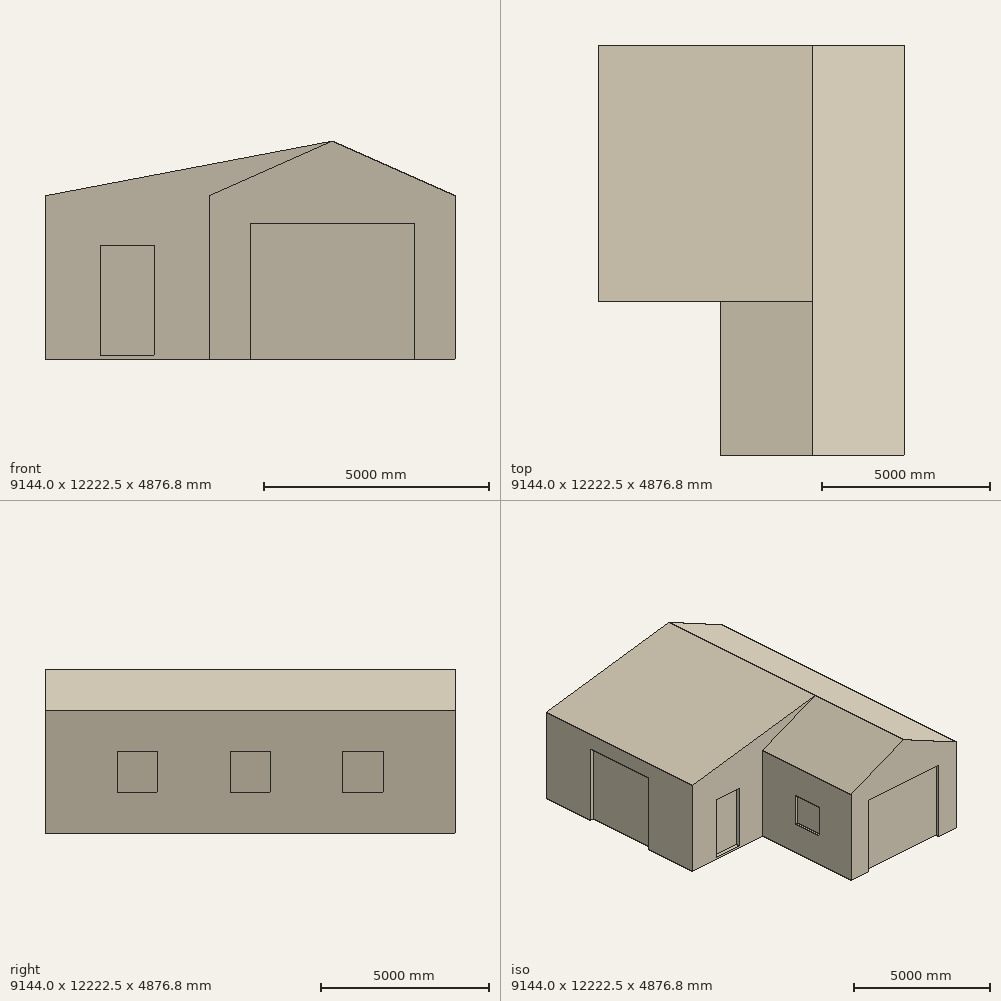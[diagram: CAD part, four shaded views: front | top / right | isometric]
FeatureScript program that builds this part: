
annotation { "Feature Type Name" : "Feature", "Feature Type Description" : "" }
export const myFeature = defineFeature(function(context is Context, id is Id, definition is map)
    precondition{}
    {
        {
            var Q0;
            Q0=qCreatedBy(makeId("Front.planeOp"),FACE);
            var sketch = newSketch(context, id + "F0", { "sketchPlane" : qUnion([Q0])});
            skLineSegment(sketch, "E0", {"start": v(0, 0) * mm, "end": v(5486.4, 0) * mm});
            skLineSegment(sketch, "E1", {"start": v(5486.4, 0) * mm, "end": v(5486.4, 3657.6) * mm});
            skLineSegment(sketch, "E2", {"start": v(5486.4, 3657.6) * mm, "end": v(2743.2, 4876.8) * mm});
            skLineSegment(sketch, "E3", {"start": v(2743.2, 4876.8) * mm, "end": v(0, 3657.6) * mm});
            skLineSegment(sketch, "E4", {"start": v(0, 3657.6) * mm, "end": v(0, 0) * mm});
            skPoint(sketch, "E5", {"position": v(2743.2, 0) * mm});
            skSolve(sketch);
        }
        {
            var Q0;
            Q0=makeQuery(id+"F0.imprint","IMPRINT",FACE,{"disambiguationData":[TD([[makeQuery(id+"F0.imprint","IMPRINT",EDGE,{"derivedFrom":sQuery(id+"F0.wireOp",EDGE,"E0")}),1.0]])]});
            extrude(context, id + "F1", {"entities" : qUnion([Q0]), "depth" : 12192 * mm, "offsetDistance" : 30.48 * mm});
        }
        {
            var Q0;
            Q0=makeQuery(id+"F1.opExtrude","SWEPT_FACE",FACE,{"disambiguationData":[OSD([sQuery(id+"F0.wireOp",EDGE,"E4")])]});
            var sketch = newSketch(context, id + "F2", { "sketchPlane" : qUnion([Q0])});
            skLineSegment(sketch, "E6", {"start": v(0, 0) * mm, "end": v(0, 3657.6) * mm});
            skLineSegment(sketch, "E7.0", {"start": v(12192, 4876.8) * mm, "end": v(3810, 4876.8) * mm});
            skLineSegment(sketch, "E8", {"start": v(7620, 3657.6) * mm, "end": v(7620, 0) * mm});
            skLineSegment(sketch, "E9", {"start": v(7620, 0) * mm, "end": v(0, 0) * mm});
            skPoint(sketch, "E10", {"position": v(3810, 0) * mm});
            skLineSegment(sketch, "E11", {"start": v(0, 3657.6) * mm, "end": v(7620, 3657.6) * mm});
            skPoint(sketch, "E12.start.orphan", {"position": v(3810, 4876.8) * mm});
            skPoint(sketch, "E13.orphan", {"position": v(0, 4876.8) * mm});
            skSolve(sketch);
        }
        {
            var Q0;
            Q0=qSketchRegion(id+"F2",true);
            extrude(context, id + "F3", {"entities" : qUnion([Q0]), "operationType" : NewBodyOperationType.ADD, "depth" : 3657.6 * mm, "offsetDistance" : 30.48 * mm, "hasSecondDirection" : true, "secondDirectionOppositeDirection" : true, "secondDirectionDepth" : 2743.2 * mm});
        }
        {
            var Q0;
            Q0=makeQuery(id+"F1.opExtrude","CAP_FACE",FACE,{"disambiguationData":[OSD([sQuery(id+"F0.wireOp",EDGE,"E0"),sQuery(id+"F0.wireOp",EDGE,"E1"),sQuery(id+"F0.wireOp",EDGE,"E2"),sQuery(id+"F0.wireOp",EDGE,"E3"),sQuery(id+"F0.wireOp",EDGE,"E4")])],"isStart":false});
            extrude(context, id + "F4", {"entities" : qUnion([Q0]), "operationType" : NewBodyOperationType.ADD, "depth" : 30.48 * mm, "offsetDistance" : 30.48 * mm});
        }
        {
            var Q0;
            Q0=makeQuery(id+"F4.opExtrude","CAP_FACE",FACE,{"disambiguationData":[OSD([sQuery(id+"F0.wireOp",EDGE,"E0"),sQuery(id+"F0.wireOp",EDGE,"E1"),sQuery(id+"F0.wireOp",EDGE,"E2"),sQuery(id+"F0.wireOp",EDGE,"E3"),sQuery(id+"F0.wireOp",EDGE,"E4")])],"isStart":false});
            var sketch = newSketch(context, id + "F5", { "sketchPlane" : qUnion([Q0])});
            skLineSegment(sketch, "E14.bottom", {"start": v(914.4, 0) * mm, "end": v(4572, 0) * mm});
            skLineSegment(sketch, "E14.top", {"start": v(914.4, 3048) * mm, "end": v(4572, 3048) * mm});
            skLineSegment(sketch, "E14.left", {"start": v(914.4, 0) * mm, "end": v(914.4, 3048) * mm});
            skLineSegment(sketch, "E14.right", {"start": v(4572, 0) * mm, "end": v(4572, 3048) * mm});
            skSolve(sketch);
        }
        {
            var Q0;
            Q0=qSketchRegion(id+"F5",true);
            extrude(context, id + "F6", {"entities" : qUnion([Q0]), "operationType" : NewBodyOperationType.REMOVE, "oppositeDirection" : true, "depth" : 152.4 * mm, "offsetDistance" : 30.48 * mm});
        }
        {
            var Q0;
            Q0=makeQuery(id+"F3.opExtrude","CAP_FACE",FACE,{"disambiguationData":[OSD([sQuery(id+"F2.wireOp",EDGE,"E6"),sQuery(id+"F2.wireOp",EDGE,"TFXyKFC6-9P5i-MGsC-qPEY-CPmH8dyxXZE2"),sQuery(id+"F2.wireOp",EDGE,"E12"),sQuery(id+"F2.wireOp",EDGE,"E8"),sQuery(id+"F2.wireOp",EDGE,"E9")])],"isStart":false});
            var sketch = newSketch(context, id + "F7", { "sketchPlane" : qUnion([Q0])});
            skLineSegment(sketch, "E15.bottom", {"start": v(2286, 0) * mm, "end": v(5334, 0) * mm});
            skLineSegment(sketch, "E15.top", {"start": v(2286, 3048) * mm, "end": v(5334, 3048) * mm});
            skLineSegment(sketch, "E15.left", {"start": v(2286, 0) * mm, "end": v(2286, 3048) * mm});
            skLineSegment(sketch, "E15.right", {"start": v(5334, 0) * mm, "end": v(5334, 3048) * mm});
            skSolve(sketch);
        }
        {
            var Q0;
            Q0=qSketchRegion(id+"F7",true);
            extrude(context, id + "F8", {"entities" : qUnion([Q0]), "operationType" : NewBodyOperationType.REMOVE, "oppositeDirection" : true, "depth" : 152.4 * mm, "offsetDistance" : 30.48 * mm});
        }
        {
            var Q0;
            Q0=makeQuery(id+"F3.opExtrude","SWEPT_FACE",FACE,{"disambiguationData":[OSD([sQuery(id+"F2.wireOp",EDGE,"E8")])]});
            var sketch = newSketch(context, id + "F9", { "sketchPlane" : qUnion([Q0])});
            skLineSegment(sketch, "E16.bottom", {"start": v(-2438.4, 100.58) * mm, "end": v(-1219.2, 100.58) * mm});
            skLineSegment(sketch, "E16.top", {"start": v(-2438.4, 2538.98) * mm, "end": v(-1219.2, 2538.98) * mm});
            skLineSegment(sketch, "E16.left", {"start": v(-2438.4, 100.58) * mm, "end": v(-2438.4, 2538.98) * mm});
            skLineSegment(sketch, "E16.right", {"start": v(-1219.2, 100.58) * mm, "end": v(-1219.2, 2538.98) * mm});
            skSolve(sketch);
        }
        {
            var Q0;
            Q0=qSketchRegion(id+"F9",true);
            extrude(context, id + "F10", {"entities" : qUnion([Q0]), "operationType" : NewBodyOperationType.REMOVE, "oppositeDirection" : true, "depth" : 152.4 * mm, "offsetDistance" : 30.48 * mm});
        }
        {
            var Q0;
            {var subQ0=sQuery(id+"F0.wireOp",EDGE,"E1");Q0=makeQuery(id+"F4.boolean.opBoolean","MERGE",FACE,{"derivedFrom":[makeQuery(id+"F1.opExtrude","SWEPT_FACE",FACE,{"disambiguationData":[OSD([subQ0])]}),makeQuery(id+"F4.opExtrude","SWEPT_FACE",FACE,{"disambiguationData":[OSD([subQ0])]})]});}
            var sketch = newSketch(context, id + "F11", { "sketchPlane" : qUnion([Q0])});
            skLineSegment(sketch, "E17.bottom", {"start": v(-10088.88, 2438.4) * mm, "end": v(-8869.68, 2438.4) * mm});
            skLineSegment(sketch, "E17.top", {"start": v(-10088.88, 1219.2) * mm, "end": v(-8869.68, 1219.2) * mm});
            skLineSegment(sketch, "E17.left", {"start": v(-10088.88, 2438.4) * mm, "end": v(-10088.88, 1219.2) * mm});
            skLineSegment(sketch, "E17.right", {"start": v(-8869.68, 2438.4) * mm, "end": v(-8869.68, 1219.2) * mm});
            skLineSegment(sketch, "E18.bottom", {"start": v(-6720.84, 2438.4) * mm, "end": v(-5501.64, 2438.4) * mm});
            skLineSegment(sketch, "E18.top", {"start": v(-6720.84, 1219.2) * mm, "end": v(-5501.64, 1219.2) * mm});
            skLineSegment(sketch, "E18.left", {"start": v(-6720.84, 2438.4) * mm, "end": v(-6720.84, 1219.2) * mm});
            skLineSegment(sketch, "E18.right", {"start": v(-5501.64, 2438.4) * mm, "end": v(-5501.64, 1219.2) * mm});
            skLineSegment(sketch, "E19.bottom", {"start": v(-3368.04, 2438.4) * mm, "end": v(-2148.84, 2438.4) * mm});
            skLineSegment(sketch, "E19.top", {"start": v(-3368.04, 1219.2) * mm, "end": v(-2148.84, 1219.2) * mm});
            skLineSegment(sketch, "E19.left", {"start": v(-3368.04, 2438.4) * mm, "end": v(-3368.04, 1219.2) * mm});
            skLineSegment(sketch, "E19.right", {"start": v(-2148.84, 2438.4) * mm, "end": v(-2148.84, 1219.2) * mm});
            skPoint(sketch, "E20", {"position": v(-6111.24, 2438.4) * mm});
            skPoint(sketch, "E21", {"position": v(-6111.24, 3657.6) * mm});
            skSolve(sketch);
        }
        {
            var Q0;
            Q0=qSketchRegion(id+"F11",true);
            extrude(context, id + "F12", {"entities" : qUnion([Q0]), "operationType" : NewBodyOperationType.REMOVE, "oppositeDirection" : true, "depth" : 100.58 * mm, "offsetDistance" : 30.48 * mm});
        }
        {
            var Q0;
            Q0=makeQuery(id+"F3.boolean.opBoolean","MERGE",FACE,{"derivedFrom":[makeQuery(id+"F1.opExtrude","CAP_FACE",FACE,{"disambiguationData":[OSD([sQuery(id+"F0.wireOp",EDGE,"E0"),sQuery(id+"F0.wireOp",EDGE,"E1"),sQuery(id+"F0.wireOp",EDGE,"E2"),sQuery(id+"F0.wireOp",EDGE,"E3"),sQuery(id+"F0.wireOp",EDGE,"E4")])],"isStart":true}),makeQuery(id+"F3.opExtrude","SWEPT_FACE",FACE,{"disambiguationData":[OSD([sQuery(id+"F2.wireOp",EDGE,"E6")])]})]});
            var sketch = newSketch(context, id + "F13", { "sketchPlane" : qUnion([Q0])});
            skLineSegment(sketch, "E22.bottom", {"start": v(-3352.8, 2438.4) * mm, "end": v(-2133.6, 2438.4) * mm});
            skLineSegment(sketch, "E22.top", {"start": v(-3352.8, 1219.2) * mm, "end": v(-2133.6, 1219.2) * mm});
            skLineSegment(sketch, "E22.left", {"start": v(-3352.8, 2438.4) * mm, "end": v(-3352.8, 1219.2) * mm});
            skLineSegment(sketch, "E22.right", {"start": v(-2133.6, 2438.4) * mm, "end": v(-2133.6, 1219.2) * mm});
            skLineSegment(sketch, "E23.bottom", {"start": v(914.4, 2438.4) * mm, "end": v(2133.6, 2438.4) * mm});
            skLineSegment(sketch, "E23.top", {"start": v(914.4, 1219.2) * mm, "end": v(2133.6, 1219.2) * mm});
            skLineSegment(sketch, "E23.left", {"start": v(914.4, 2438.4) * mm, "end": v(914.4, 1219.2) * mm});
            skLineSegment(sketch, "E23.right", {"start": v(2133.6, 2438.4) * mm, "end": v(2133.6, 1219.2) * mm});
            skPoint(sketch, "E24", {"position": v(-2743.2, 2438.4) * mm});
            skPoint(sketch, "E25", {"position": v(-2743.2, 4876.8) * mm});
            skSolve(sketch);
        }
        {
            var Q0;
            Q0=qSketchRegion(id+"F13",true);
            extrude(context, id + "F14", {"entities" : qUnion([Q0]), "operationType" : NewBodyOperationType.REMOVE, "oppositeDirection" : true, "depth" : 100.58 * mm, "offsetDistance" : 30.48 * mm});
        }
        {
            var Q0;
            {var subQ0=sQuery(id+"F0.wireOp",EDGE,"E4");Q0=makeQuery(id+"F4.boolean.opBoolean","MERGE",FACE,{"derivedFrom":[makeQuery(id+"F1.opExtrude","SWEPT_FACE",FACE,{"disambiguationData":[OSD([subQ0])]}),makeQuery(id+"F4.opExtrude","SWEPT_FACE",FACE,{"disambiguationData":[OSD([subQ0])]})]});}
            var sketch = newSketch(context, id + "F15", { "sketchPlane" : qUnion([Q0])});
            skLineSegment(sketch, "E26.bottom", {"start": v(9326.88, 2438.4) * mm, "end": v(10546.08, 2438.4) * mm});
            skLineSegment(sketch, "E26.top", {"start": v(9326.88, 1219.2) * mm, "end": v(10546.08, 1219.2) * mm});
            skLineSegment(sketch, "E26.left", {"start": v(9326.88, 2438.4) * mm, "end": v(9326.88, 1219.2) * mm});
            skLineSegment(sketch, "E26.right", {"start": v(10546.08, 2438.4) * mm, "end": v(10546.08, 1219.2) * mm});
            skSolve(sketch);
        }
        {
            var Q0;
            Q0=qSketchRegion(id+"F15",true);
            extrude(context, id + "F16", {"entities" : qUnion([Q0]), "operationType" : NewBodyOperationType.REMOVE, "oppositeDirection" : true, "depth" : 100.58 * mm, "offsetDistance" : 30.48 * mm});
        }
        {
            var Q0;
            Q0=makeQuery(id+"F3.boolean.opBoolean","MERGE",FACE,{"derivedFrom":[makeQuery(id+"F1.opExtrude","CAP_FACE",FACE,{"disambiguationData":[OSD([sQuery(id+"F0.wireOp",EDGE,"E0"),sQuery(id+"F0.wireOp",EDGE,"E1"),sQuery(id+"F0.wireOp",EDGE,"E2"),sQuery(id+"F0.wireOp",EDGE,"E3"),sQuery(id+"F0.wireOp",EDGE,"E4")])],"isStart":true}),makeQuery(id+"F3.opExtrude","SWEPT_FACE",FACE,{"disambiguationData":[OSD([sQuery(id+"F2.wireOp",EDGE,"E6")])]})]});
            var sketch = newSketch(context, id + "F17", { "sketchPlane" : qUnion([Q0])});
            skLineSegment(sketch, "E27", {"start": v(-2743.2, 4876.8) * mm, "end": v(3657.6, 3657.6) * mm});
            skLineSegment(sketch, "E28", {"start": v(3657.6, 3657.6) * mm, "end": v(0, 3657.6) * mm});
            skLineSegment(sketch, "E29", {"start": v(0, 3657.6) * mm, "end": v(-2743.2, 4876.8) * mm});
            skSolve(sketch);
        }
        {
            var Q0;
            Q0 = qSketchRegion(id + "F17", true);
            extrude(context, id + "F18", {"entities" : qUnion([Q0]), "operationType" : NewBodyOperationType.ADD, "oppositeDirection" : true, "depth" : 7620 * mm, "offsetDistance" : 30.48 * mm});
        }
    });
